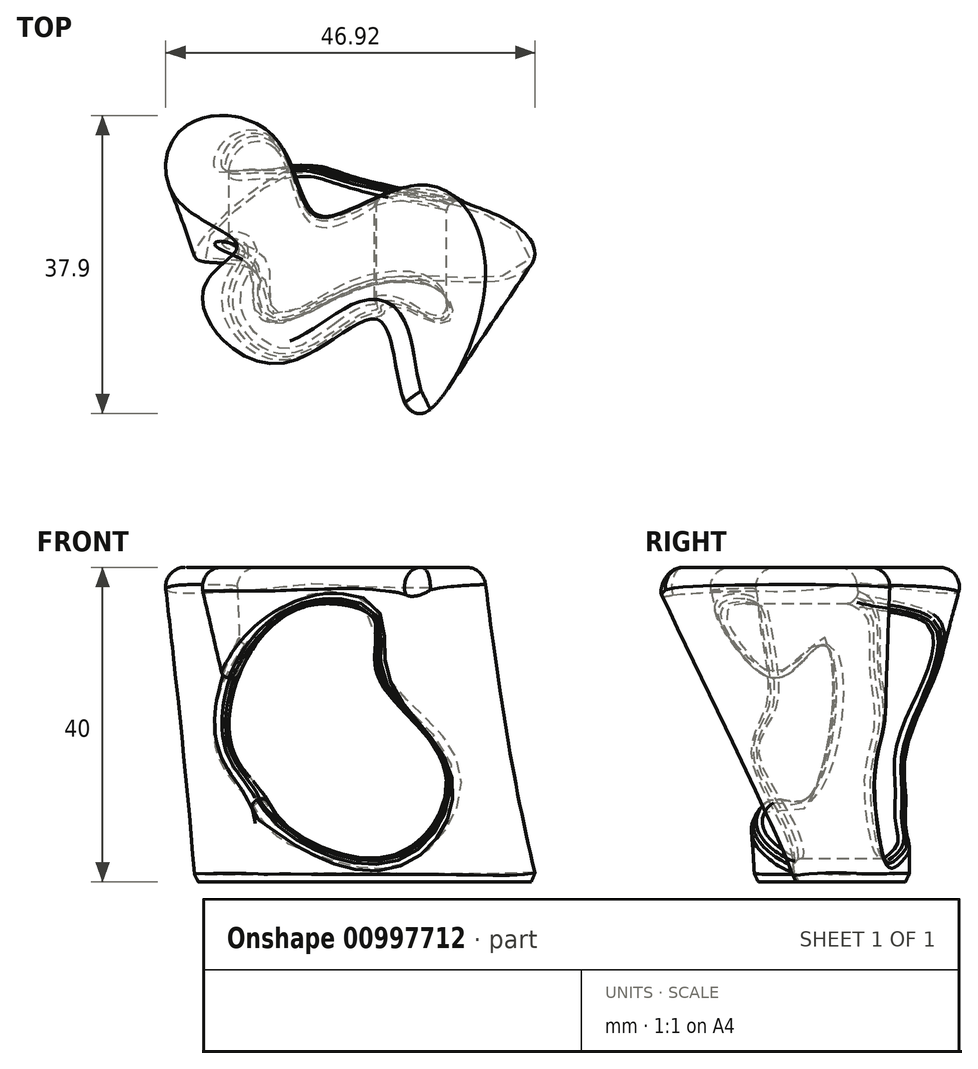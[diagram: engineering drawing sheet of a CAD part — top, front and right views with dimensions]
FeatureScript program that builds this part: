
annotation { "Feature Type Name" : "Feature", "Feature Type Description" : "" }
export const myFeature = defineFeature(function(context is Context, id is Id, definition is map)
    precondition{}
    {
        {
            var Q0;
            Q0=qCreatedBy(makeId("Top.planeOp"),FACE);
            var sketch = newSketch(context, id + "F0", { "sketchPlane" : qUnion([Q0])});
            skFitSpline(sketch, "E0", {"points": [v(0, 0) * mm, v(10.25, 6.76) * mm, v(17.53, 5.26) * mm, v(36, 0) * mm, v(39.8, -4.33) * mm, v(35.25, -7.42) * mm, v(17.36, -8.53) * mm, v(6.46, -12.57) * mm, v(4.02, -6.68) * mm, v(-3.42, -5.27) * mm, v(0, 0) * mm]});
            skSolve(sketch);
        }
        {
            var Q0;
            Q0=qCreatedBy(makeId("Top.planeOp"),FACE);
            cPlane(context, id + "F1", {"entities" : qUnion([Q0]), "cplaneType" : CPlaneType.OFFSET, "offset" : 40 * mm, "width" : 150 * mm, "height" : 150 * mm});
        }
        {
            var Q0;
            Q0=qCreatedBy(id+"F1.planeOp",FACE);
            var sketch = newSketch(context, id + "F2", { "sketchPlane" : qUnion([Q0])});
            skFitSpline(sketch, "E1", {"points": [v(6.38, 10.62) * mm, v(11.7, 0) * mm, v(25.28, 4.44) * mm, v(32.84, -9.3) * mm, v(22.87, -26.15) * mm, v(19.44, -13.26) * mm, v(6.55, -18.93) * mm, v(-3.25, -8.96) * mm, v(1.65, -3.2) * mm, v(-6.17, 3.06) * mm, v(-5.3, 12.69) * mm, v(6.38, 10.62) * mm]});
            skSolve(sketch);
        }
        {
            var Q0;
            Q0=makeQuery(id+"F2.imprint","IMPRINT",FACE,{"disambiguationData":[TD([[makeQuery(id+"F2.imprint","IMPRINT",EDGE,{"derivedFrom":sQuery(id+"F2.wireOp",EDGE,"E1")}),-1.0]])]});
            var Q1;
            Q1=makeQuery(id+"F0.imprint","IMPRINT",FACE,{"disambiguationData":[TD([[makeQuery(id+"F0.imprint","IMPRINT",EDGE,{"derivedFrom":sQuery(id+"F0.wireOp",EDGE,"E0")}),-1.0]])]});
            loft(context, id + "F3", {"sheetProfilesArray" : [{ "sheetProfileEntities" : qUnion([Q0]) }, { "sheetProfileEntities" : qUnion([Q1]) }]});
        }
        {
            var Q0;
            Q0=qCreatedBy(makeId("Front.planeOp"),FACE);
            var sketch = newSketch(context, id + "F4", { "sketchPlane" : qUnion([Q0])});
            skFitSpline(sketch, "E2", {"points": [v(15.05, 35.23) * mm, v(8.92, 34.44) * mm, v(2.54, 27.64) * mm, v(1.14, 16.82) * mm, v(4.9, 11.42) * mm, v(7.76, 7.35) * mm, v(21.5, 3.4) * mm, v(28.12, 14.33) * mm, v(19.55, 26.18) * mm, v(19.18, 33.1) * mm, v(15.05, 35.23) * mm]});
            skSolve(sketch);
        }
        {
            var Q0;
            Q0 = qSketchRegion(id + "F4", true);
            extrude(context, id + "F5", {"entities" : qUnion([Q0]), "operationType" : NewBodyOperationType.REMOVE, "endBound" : BoundingType.THROUGH_ALL, "oppositeDirection" : true, "depth" : 25 * mm, "offsetDistance" : 25 * mm, "hasSecondDirection" : true, "secondDirectionBound" : SecondDirectionBoundingType.THROUGH_ALL, "secondDirectionOppositeDirection" : false, "secondDirectionDepth" : 25 * mm});
        }
        {
            var Q0;
            Q0=makeQuery(id+"F3.opLoft","CAP_FACE",FACE,{"disambiguationData":[OSD([makeQuery(id+"F2.imprint","IMPRINT",FACE,{"disambiguationData":[TD([[makeQuery(id+"F2.imprint","IMPRINT",EDGE,{"derivedFrom":sQuery(id+"F2.wireOp",EDGE,"E1")}),-1.0]])]})])],"isStart":true});
            fillet(context, id + "F6", {"entities" : qUnion([Q0]), "radius" : 2.5 * mm, "tangentPropagation" : true, "allowEdgeOverflow" : false});
        }
        {
            var Q0;
            Q0=makeQuery(id+"F3.opLoft","MID_CAP_EDGE",EDGE,{"disambiguationData":[OSD([sQuery(id+"F0.wireOp",EDGE,"E0")])],"capPos":1.0});
            chamfer(context, id + "F7", {"entities" : qUnion([Q0]), "chamferType" : ChamferType.OFFSET_ANGLE, "width" : 1 * mm, "oppositeDirection" : true, "angle" : 20 * degree, "tangentPropagation" : true});
        }
        {
            var Q0;
            Q0=makeQuery(id+"F5.boolean.opBoolean","INTERSECT",EDGE,{"disambiguationData":[OD(0.0)],"derivedFrom":[makeQuery(id+"F3.opLoft","SWEPT_FACE",FACE,{"disambiguationData":[OSD([sQuery(id+"F0.wireOp",EDGE,"E0"),sQuery(id+"F2.wireOp",EDGE,"E1")])]}),makeQuery(id+"F5.opExtrude","SWEPT_FACE",FACE,{"disambiguationData":[OSD([sQuery(id+"F4.wireOp",EDGE,"E2")])]})]});
            var Q1;
            Q1=makeQuery(id+"F5.boolean.opBoolean","INTERSECT",EDGE,{"disambiguationData":[OD(1.0)],"derivedFrom":[makeQuery(id+"F3.opLoft","SWEPT_FACE",FACE,{"disambiguationData":[OSD([sQuery(id+"F0.wireOp",EDGE,"E0"),sQuery(id+"F2.wireOp",EDGE,"E1")])]}),makeQuery(id+"F5.opExtrude","SWEPT_FACE",FACE,{"disambiguationData":[OSD([sQuery(id+"F4.wireOp",EDGE,"E2")])]})]});
            chamfer(context, id + "F8", {"entities" : qUnion([Q0, Q1]), "width" : 1 * mm, "tangentPropagation" : true});
        }
        {
            var Q0;
            {var subQ0=makeQuery(id+"F3.opLoft","SWEPT_FACE",FACE,{"disambiguationData":[OSD([sQuery(id+"F0.wireOp",EDGE,"E0"),sQuery(id+"F2.wireOp",EDGE,"E1")])]});Q0=makeQuery(id+"F8.opChamfer","BLEND_EDGE",EDGE,{"blendedFrom":[makeQuery(id+"F5.boolean.opBoolean","INTERSECT",EDGE,{"disambiguationData":[OD(1.0)],"derivedFrom":[subQ0,makeQuery(id+"F5.opExtrude","SWEPT_FACE",FACE,{"disambiguationData":[OSD([sQuery(id+"F4.wireOp",EDGE,"E2")])]})]}),subQ0],"blendedInto":[subQ0]});}
            var Q1;
            {var subQ0=makeQuery(id+"F5.opExtrude","SWEPT_FACE",FACE,{"disambiguationData":[OSD([sQuery(id+"F4.wireOp",EDGE,"E2")])]});Q1=makeQuery(id+"F8.opChamfer","BLEND_EDGE",EDGE,{"blendedFrom":[makeQuery(id+"F5.boolean.opBoolean","INTERSECT",EDGE,{"disambiguationData":[OD(1.0)],"derivedFrom":[makeQuery(id+"F3.opLoft","SWEPT_FACE",FACE,{"disambiguationData":[OSD([sQuery(id+"F0.wireOp",EDGE,"E0"),sQuery(id+"F2.wireOp",EDGE,"E1")])]}),subQ0]}),makeQuery(id+"F5.boolean.opBoolean","COPY",FACE,{"derivedFrom":subQ0})],"blendedInto":[makeQuery(id+"F5.boolean.opBoolean","COPY",FACE,{"derivedFrom":subQ0})]});}
            var Q2;
            {var subQ0=makeQuery(id+"F3.opLoft","SWEPT_FACE",FACE,{"disambiguationData":[OSD([sQuery(id+"F0.wireOp",EDGE,"E0"),sQuery(id+"F2.wireOp",EDGE,"E1")])]});Q2=makeQuery(id+"F8.opChamfer","BLEND_EDGE",EDGE,{"blendedFrom":[makeQuery(id+"F5.boolean.opBoolean","INTERSECT",EDGE,{"disambiguationData":[OD(0.0)],"derivedFrom":[subQ0,makeQuery(id+"F5.opExtrude","SWEPT_FACE",FACE,{"disambiguationData":[OSD([sQuery(id+"F4.wireOp",EDGE,"E2")])]})]}),subQ0],"blendedInto":[subQ0]});}
            var Q3;
            {var subQ0=makeQuery(id+"F5.opExtrude","SWEPT_FACE",FACE,{"disambiguationData":[OSD([sQuery(id+"F4.wireOp",EDGE,"E2")])]});Q3=makeQuery(id+"F8.opChamfer","BLEND_EDGE",EDGE,{"blendedFrom":[makeQuery(id+"F5.boolean.opBoolean","INTERSECT",EDGE,{"disambiguationData":[OD(0.0)],"derivedFrom":[makeQuery(id+"F3.opLoft","SWEPT_FACE",FACE,{"disambiguationData":[OSD([sQuery(id+"F0.wireOp",EDGE,"E0"),sQuery(id+"F2.wireOp",EDGE,"E1")])]}),subQ0]}),makeQuery(id+"F5.boolean.opBoolean","COPY",FACE,{"derivedFrom":subQ0})],"blendedInto":[makeQuery(id+"F5.boolean.opBoolean","COPY",FACE,{"derivedFrom":subQ0})]});}
            fillet(context, id + "F9", {"entities" : qUnion([Q0, Q1, Q2, Q3]), "radius" : 1 * mm, "tangentPropagation" : true, "allowEdgeOverflow" : false});
        }
    });
